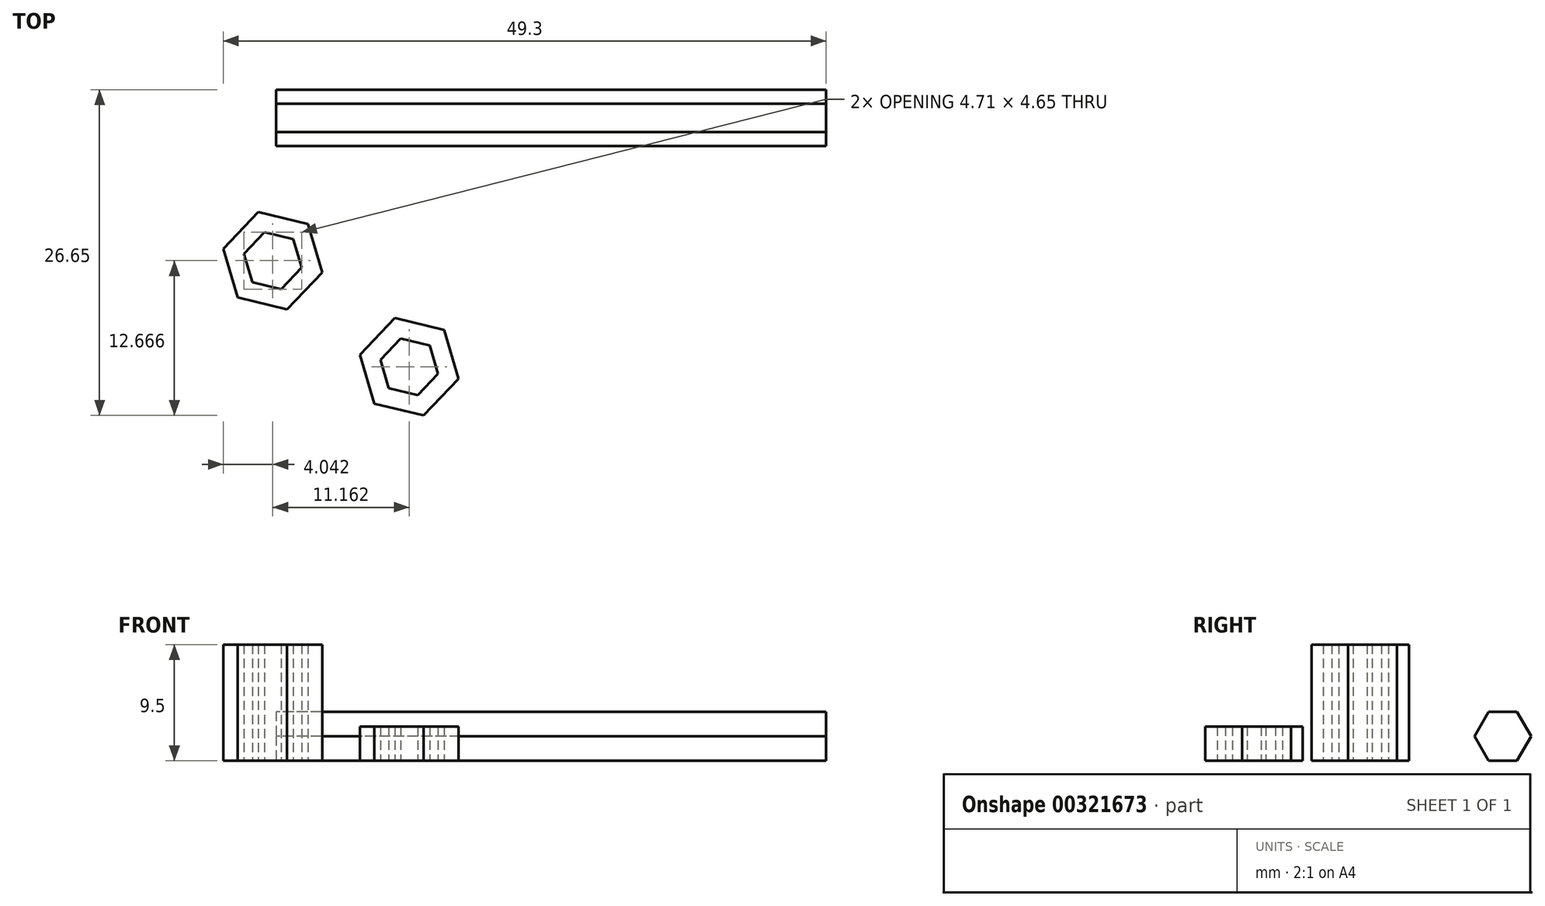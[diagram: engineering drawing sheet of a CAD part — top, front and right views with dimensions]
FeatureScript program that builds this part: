
annotation { "Feature Type Name" : "Feature", "Feature Type Description" : "" }
export const myFeature = defineFeature(function(context is Context, id is Id, definition is map)
    precondition{}
    {
        {
            var Q0;
            Q0=qCreatedBy(makeId("Right.planeOp"),FACE);
            var sketch = newSketch(context, id + "F0", { "sketchPlane" : qUnion([Q0])});
            skCircle(sketch, "E0.cCircle", {"center": v(11.92, 2) * mm, "radius": 2 * mm, "construction": true});
            skLineSegment(sketch, "E0.0", {"start": v(14.23, 2) * mm, "end": v(13.07, 0) * mm});
            skLineSegment(sketch, "E0.1", {"start": v(13.07, 0) * mm, "end": v(10.77, 0) * mm});
            skLineSegment(sketch, "E0.2", {"start": v(10.77, 0) * mm, "end": v(9.61, 2) * mm});
            skLineSegment(sketch, "E0.3", {"start": v(9.61, 2) * mm, "end": v(10.77, 4) * mm});
            skLineSegment(sketch, "E0.4", {"start": v(10.77, 4) * mm, "end": v(13.07, 4) * mm});
            skLineSegment(sketch, "E0.5", {"start": v(13.07, 4) * mm, "end": v(14.23, 2) * mm});
            skPoint(sketch, "E0.0.midPoint", {"position": v(13.65, 1) * mm});
            skSolve(sketch);
        }
        {
            var Q0;
            Q0 = qSketchRegion(id + "F0", true);
            extrude(context, id + "F1", {"entities" : qUnion([Q0]), "depth" : 45 * mm});
        }
        {
            var Q0;
            Q0=qCreatedBy(makeId("Top.planeOp"),FACE);
            var sketch = newSketch(context, id + "F2", { "sketchPlane" : qUnion([Q0])});
            skCircle(sketch, "E1.cCircle", {"center": v(10.9, -8.44) * mm, "radius": 3.6 * mm, "construction": true});
            skLineSegment(sketch, "E1.0", {"start": v(14.94, -9.41) * mm, "end": v(12.08, -12.42) * mm});
            skLineSegment(sketch, "E1.1", {"start": v(12.08, -12.42) * mm, "end": v(8.04, -11.45) * mm});
            skLineSegment(sketch, "E1.2", {"start": v(8.04, -11.45) * mm, "end": v(6.86, -7.46) * mm});
            skLineSegment(sketch, "E1.3", {"start": v(6.86, -7.46) * mm, "end": v(9.73, -4.45) * mm});
            skLineSegment(sketch, "E1.4", {"start": v(9.73, -4.45) * mm, "end": v(13.77, -5.42) * mm});
            skLineSegment(sketch, "E1.5", {"start": v(13.77, -5.42) * mm, "end": v(14.94, -9.41) * mm});
            skPoint(sketch, "E1.0.midPoint", {"position": v(13.51, -10.92) * mm});
            skCircle(sketch, "E2.cCircle", {"center": v(10.9, -8.44) * mm, "radius": 2.1 * mm, "construction": true});
            skLineSegment(sketch, "E2.0", {"start": v(13.26, -9) * mm, "end": v(11.59, -10.76) * mm});
            skLineSegment(sketch, "E2.1", {"start": v(11.59, -10.76) * mm, "end": v(9.23, -10.2) * mm});
            skLineSegment(sketch, "E2.2", {"start": v(9.23, -10.2) * mm, "end": v(8.55, -7.87) * mm});
            skLineSegment(sketch, "E2.3", {"start": v(8.55, -7.87) * mm, "end": v(10.22, -6.1) * mm});
            skLineSegment(sketch, "E2.4", {"start": v(10.22, -6.1) * mm, "end": v(12.57, -6.68) * mm});
            skLineSegment(sketch, "E2.5", {"start": v(12.57, -6.68) * mm, "end": v(13.26, -9) * mm});
            skPoint(sketch, "E2.0.midPoint", {"position": v(12.43, -9.88) * mm});
            skSolve(sketch);
        }
        {
            var Q0;
            Q0 = qSketchRegion(id + "F2", true);
            extrude(context, id + "F3", {"entities" : qUnion([Q0]), "depth" : 2.8 * mm});
        }
        {
            var Q0;
            Q0=qCreatedBy(makeId("Top.planeOp"),FACE);
            var sketch = newSketch(context, id + "F4", { "sketchPlane" : qUnion([Q0])});
            skCircle(sketch, "E3.cCircle", {"center": v(-0.26, 0.25) * mm, "radius": 3.6 * mm, "construction": true});
            skLineSegment(sketch, "E3.0", {"start": v(3.78, -0.73) * mm, "end": v(0.92, -3.74) * mm});
            skLineSegment(sketch, "E3.1", {"start": v(0.92, -3.74) * mm, "end": v(-3.12, -2.77) * mm});
            skLineSegment(sketch, "E3.2", {"start": v(-3.12, -2.77) * mm, "end": v(-4.3, 1.22) * mm});
            skLineSegment(sketch, "E3.3", {"start": v(-4.3, 1.22) * mm, "end": v(-1.43, 4.23) * mm});
            skLineSegment(sketch, "E3.4", {"start": v(-1.43, 4.23) * mm, "end": v(2.6, 3.26) * mm});
            skLineSegment(sketch, "E3.5", {"start": v(2.6, 3.26) * mm, "end": v(3.78, -0.73) * mm});
            skPoint(sketch, "E3.0.midPoint", {"position": v(2.35, -2.24) * mm});
            skCircle(sketch, "E4.cCircle", {"center": v(-0.26, 0.25) * mm, "radius": 2.1 * mm, "construction": true});
            skLineSegment(sketch, "E4.0", {"start": v(2.1, -0.32) * mm, "end": v(0.43, -2.08) * mm});
            skLineSegment(sketch, "E4.1", {"start": v(0.43, -2.08) * mm, "end": v(-1.93, -1.51) * mm});
            skLineSegment(sketch, "E4.2", {"start": v(-1.93, -1.51) * mm, "end": v(-2.62, 0.81) * mm});
            skLineSegment(sketch, "E4.3", {"start": v(-2.62, 0.81) * mm, "end": v(-0.94, 2.57) * mm});
            skLineSegment(sketch, "E4.4", {"start": v(-0.94, 2.57) * mm, "end": v(1.41, 2) * mm});
            skLineSegment(sketch, "E4.5", {"start": v(1.41, 2) * mm, "end": v(2.1, -0.32) * mm});
            skPoint(sketch, "E4.0.midPoint", {"position": v(1.26, -1.2) * mm});
            skSolve(sketch);
        }
        {
            var Q0;
            Q0 = qSketchRegion(id + "F4", true);
            extrude(context, id + "F5", {"entities" : qUnion([Q0]), "depth" : 9.5 * mm});
        }
    });
